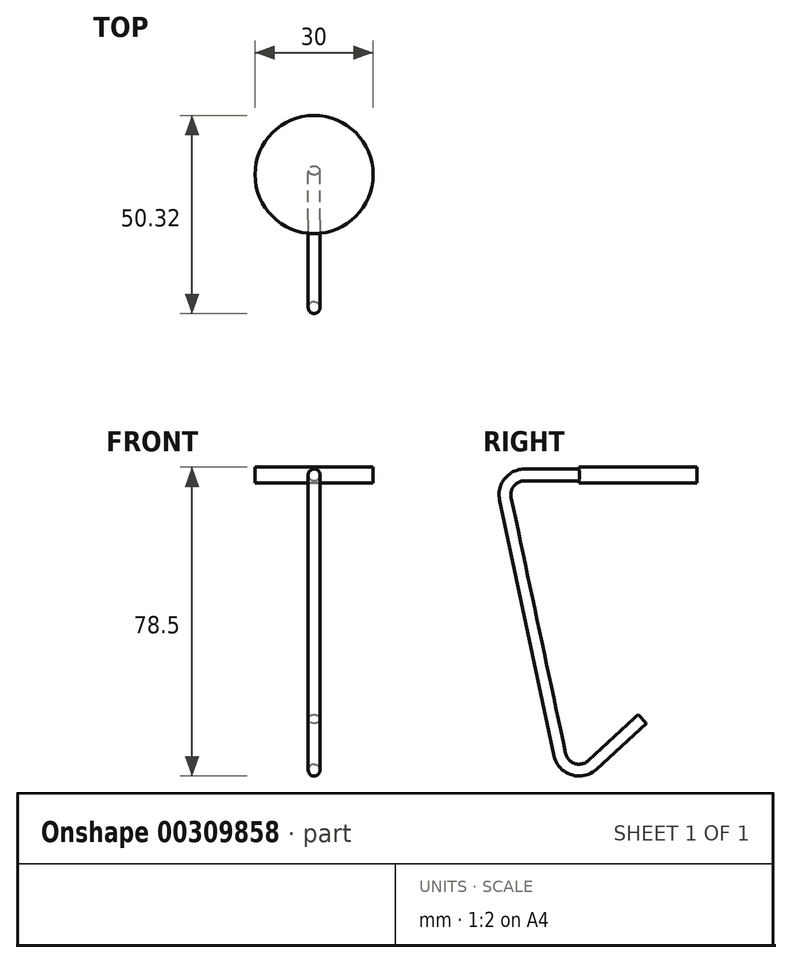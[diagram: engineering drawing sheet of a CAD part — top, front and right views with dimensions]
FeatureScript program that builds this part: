
annotation { "Feature Type Name" : "Feature", "Feature Type Description" : "" }
export const myFeature = defineFeature(function(context is Context, id is Id, definition is map)
    precondition{}
    {
        {
            var Q0;
            Q0=qCreatedBy(makeId("Top.planeOp"),FACE);
            var sketch = newSketch(context, id + "F0", { "sketchPlane" : qUnion([Q0])});
            skCircle(sketch, "E0", {"center": v(0, 0) * mm, "radius": 15 * mm});
            skSolve(sketch);
        }
        {
            var Q0;
            Q0=makeQuery(id+"F0.imprint","IMPRINT",FACE,{"disambiguationData":[TD([[makeQuery(id+"F0.imprint","IMPRINT",EDGE,{"derivedFrom":sQuery(id+"F0.wireOp",EDGE,"E0")}),1.0]])]});
            extrude(context, id + "F1", {"entities" : qUnion([Q0]), "depth" : 4 * mm});
        }
        {
            var Q0;
            Q0=qCreatedBy(makeId("Front.planeOp"),FACE);
            var sketch = newSketch(context, id + "F2", { "sketchPlane" : qUnion([Q0])});
            skCircle(sketch, "E1", {"center": v(0, 2) * mm, "radius": 1.5 * mm});
            skLineSegment(sketch, "E2", {"start": v(0, 4) * mm, "end": v(0, 0) * mm, "construction": true});
            skSolve(sketch);
        }
        {
            var Q0;
            Q0=qCreatedBy(makeId("Right.planeOp"),FACE);
            var sketch = newSketch(context, id + "F3", { "sketchPlane" : qUnion([Q0])});
            skLineSegment(sketch, "E3", {"start": v(0, 2) * mm, "end": v(-28.82, 2) * mm});
            skLineSegment(sketch, "E4", {"start": v(-33.72, -4.04) * mm, "end": v(-19.9, -69.04) * mm});
            skLineSegment(sketch, "E5", {"start": v(-11.6, -71.68) * mm, "end": v(1.05, -60) * mm});
            skPoint(sketch, "E6.visualSharp", {"position": v(-35, 2) * mm});
            skArc(sketch, "E6.filletArc", {"start": v(-28.82, 2) * mm, "mid": v(-32.71, 0.15) * mm, "end": v(-33.72, -4.04) * mm});
            skPoint(sketch, "E7.visualSharp", {"position": v(-18.06, -77.63) * mm});
            skArc(sketch, "E7.filletArc", {"start": v(-19.9, -69.04) * mm, "mid": v(-16.52, -72.76) * mm, "end": v(-11.6, -71.68) * mm});
            skSolve(sketch);
        }
        {
            var Q0;
            Q0 = qSketchRegion(id + "F2", true);
            var Q1;
            Q1 = qConstructionFilter(qBodyType(qCreatedBy(id + "F3" ,EDGE), BodyType.WIRE), ConstructionObject.NO);
            sweep(context, id + "F4", {"operationType" : NewBodyOperationType.ADD, "profiles" : qUnion([Q0]), "path" : qUnion([Q1])});
        }
    });
